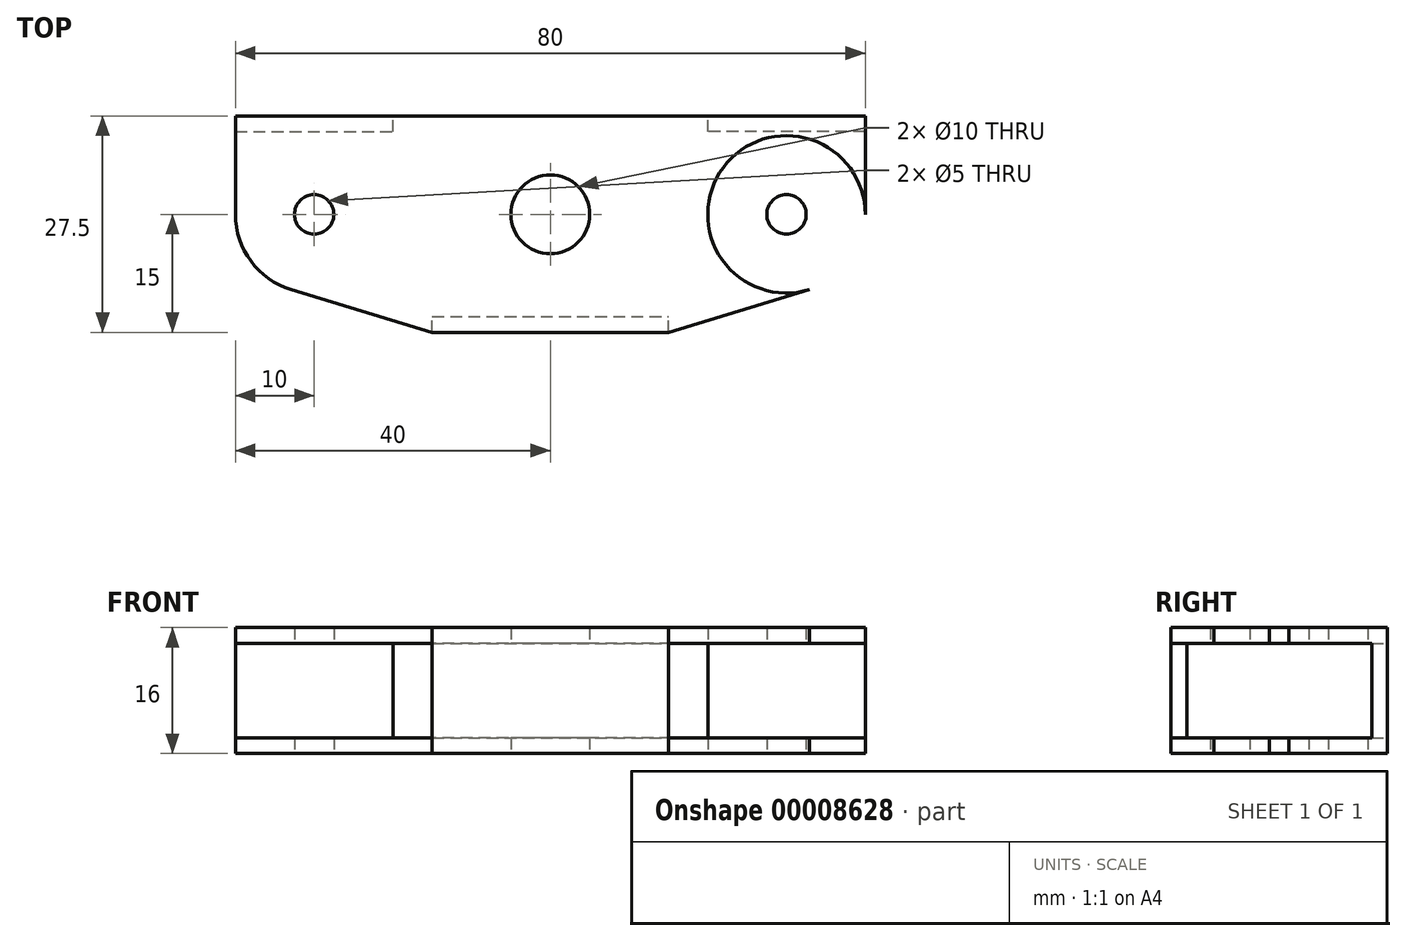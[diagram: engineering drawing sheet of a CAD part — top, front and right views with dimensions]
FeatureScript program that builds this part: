
annotation { "Feature Type Name" : "Feature", "Feature Type Description" : "" }
export const myFeature = defineFeature(function(context is Context, id is Id, definition is map)
    precondition{}
    {
        {
            var Q0;
            Q0=qCreatedBy(makeId("Top.planeOp"),FACE);
            var sketch = newSketch(context, id + "F0", { "sketchPlane" : qUnion([Q0])});
            skCircle(sketch, "E0", {"center": v(0, 0) * mm, "radius": 5 * mm});
            skCircle(sketch, "E1", {"center": v(-30, 0) * mm, "radius": 2.5 * mm});
            skLineSegment(sketch, "E2", {"start": v(0, 27.4) * mm, "end": v(0, -27.48) * mm, "construction": true});
            skCircle(sketch, "E3.MirrorC", {"center": v(30, 0) * mm, "radius": 2.5 * mm});
            skCircle(sketch, "E4", {"center": v(-30, 0) * mm, "radius": 10 * mm});
            skCircle(sketch, "E5.MirrorC", {"center": v(30, 0) * mm, "radius": 10 * mm});
            skLineSegment(sketch, "E6", {"start": v(-40, 0) * mm, "end": v(-40, 12.5) * mm});
            skLineSegment(sketch, "E7", {"start": v(-40, 12.5) * mm, "end": v(0, 12.5) * mm});
            skLineSegment(sketch, "E8", {"start": v(0, -15) * mm, "end": v(-15, -15) * mm});
            skLineSegment(sketch, "E9", {"start": v(-15, -15) * mm, "end": v(-32.9, -9.57) * mm});
            skLineSegment(sketch, "E10.MirrorCS", {"start": v(40, 12.5) * mm, "end": v(0, 12.5) * mm});
            skLineSegment(sketch, "E11.MirrorCS", {"start": v(40, 0) * mm, "end": v(40, 12.5) * mm});
            skLineSegment(sketch, "E12.MirrorCS", {"start": v(15, -15) * mm, "end": v(32.9, -9.57) * mm});
            skLineSegment(sketch, "E13.MirrorCS", {"start": v(0, -15) * mm, "end": v(15, -15) * mm});
            skLineSegment(sketch, "E14", {"start": v(-15, -15) * mm, "end": v(-15, -13) * mm});
            skLineSegment(sketch, "E15", {"start": v(-15, -13) * mm, "end": v(0, -13) * mm});
            skLineSegment(sketch, "E16.MirrorCS", {"start": v(15, -13) * mm, "end": v(0, -13) * mm});
            skLineSegment(sketch, "E17.MirrorCS", {"start": v(15, -15) * mm, "end": v(15, -13) * mm});
            skLineSegment(sketch, "E18", {"start": v(-40, 10.5) * mm, "end": v(-20, 10.5) * mm});
            skLineSegment(sketch, "E19", {"start": v(-20, 10.5) * mm, "end": v(-20, 12.5) * mm});
            skLineSegment(sketch, "E20.MirrorCS", {"start": v(20, 10.5) * mm, "end": v(20, 12.5) * mm});
            skLineSegment(sketch, "E21.MirrorCS", {"start": v(40, 10.5) * mm, "end": v(20, 10.5) * mm});
            skSolve(sketch);
        }
        {
            var Q0;
            {var subQ1=sQuery(id+"F0.wireOp",EDGE,"E18");Q0=makeQuery(id+"F0.imprint","IMPRINT",FACE,{"disambiguationData":[TD([[makeQuery(id+"F0.imprint","IMPRINT",EDGE,{"derivedFrom":subQ1}),1.0]])]});}
            var Q1;
            Q1=makeQuery(id+"F0.imprint","IMPRINT",FACE,{"disambiguationData":[TD([[makeQuery(id+"F0.imprint","IMPRINT",EDGE,{"derivedFrom":sQuery(id+"F0.wireOp",EDGE,"E0")}),-1.0]])]});
            var Q2;
            Q2=makeQuery(id+"F0.imprint","IMPRINT",FACE,{"disambiguationData":[TD([[makeQuery(id+"F0.imprint","IMPRINT",EDGE,{"derivedFrom":sQuery(id+"F0.wireOp",EDGE,"E1")}),-1.0]])]});
            var Q3;
            Q3=makeQuery(id+"F0.imprint","IMPRINT",FACE,{"disambiguationData":[TD([[makeQuery(id+"F0.imprint","IMPRINT",EDGE,{"derivedFrom":sQuery(id+"F0.wireOp",EDGE,"E3.MirrorC")}),1.0]])]});
            var Q4;
            Q4=makeQuery(id+"F0.imprint","IMPRINT",FACE,{"disambiguationData":[TD([[makeQuery(id+"F0.imprint","IMPRINT",EDGE,{"derivedFrom":sQuery(id+"F0.wireOp",EDGE,"E8")}),-1.0]])]});
            var Q5;
            {var subQ1=sQuery(id+"F0.wireOp",EDGE,"E20.MirrorCS");Q5=makeQuery(id+"F0.imprint","IMPRINT",FACE,{"disambiguationData":[TD([[makeQuery(id+"F0.imprint","IMPRINT",EDGE,{"derivedFrom":subQ1}),-1.0]])]});}
            extrude(context, id + "F1", {"entities" : qUnion([Q0, Q1, Q2, Q3, Q4, Q5]), "depth" : 16 * mm, "symmetric" : true});
        }
        {
            var Q0;
            Q0=makeQuery(id+"F0.imprint","IMPRINT",FACE,{"disambiguationData":[TD([[makeQuery(id+"F0.imprint","IMPRINT",EDGE,{"derivedFrom":sQuery(id+"F0.wireOp",EDGE,"E0")}),-1.0]])]});
            var Q1;
            Q1=makeQuery(id+"F0.imprint","IMPRINT",FACE,{"disambiguationData":[TD([[makeQuery(id+"F0.imprint","IMPRINT",EDGE,{"derivedFrom":sQuery(id+"F0.wireOp",EDGE,"E1")}),-1.0]])]});
            var Q2;
            Q2=makeQuery(id+"F0.imprint","IMPRINT",FACE,{"disambiguationData":[TD([[makeQuery(id+"F0.imprint","IMPRINT",EDGE,{"derivedFrom":sQuery(id+"F0.wireOp",EDGE,"E3.MirrorC")}),1.0]])]});
            extrude(context, id + "F2", {"entities" : qUnion([Q0, Q1, Q2]), "operationType" : NewBodyOperationType.REMOVE, "oppositeDirection" : true, "depth" : 12 * mm, "symmetric" : true});
        }
    });
